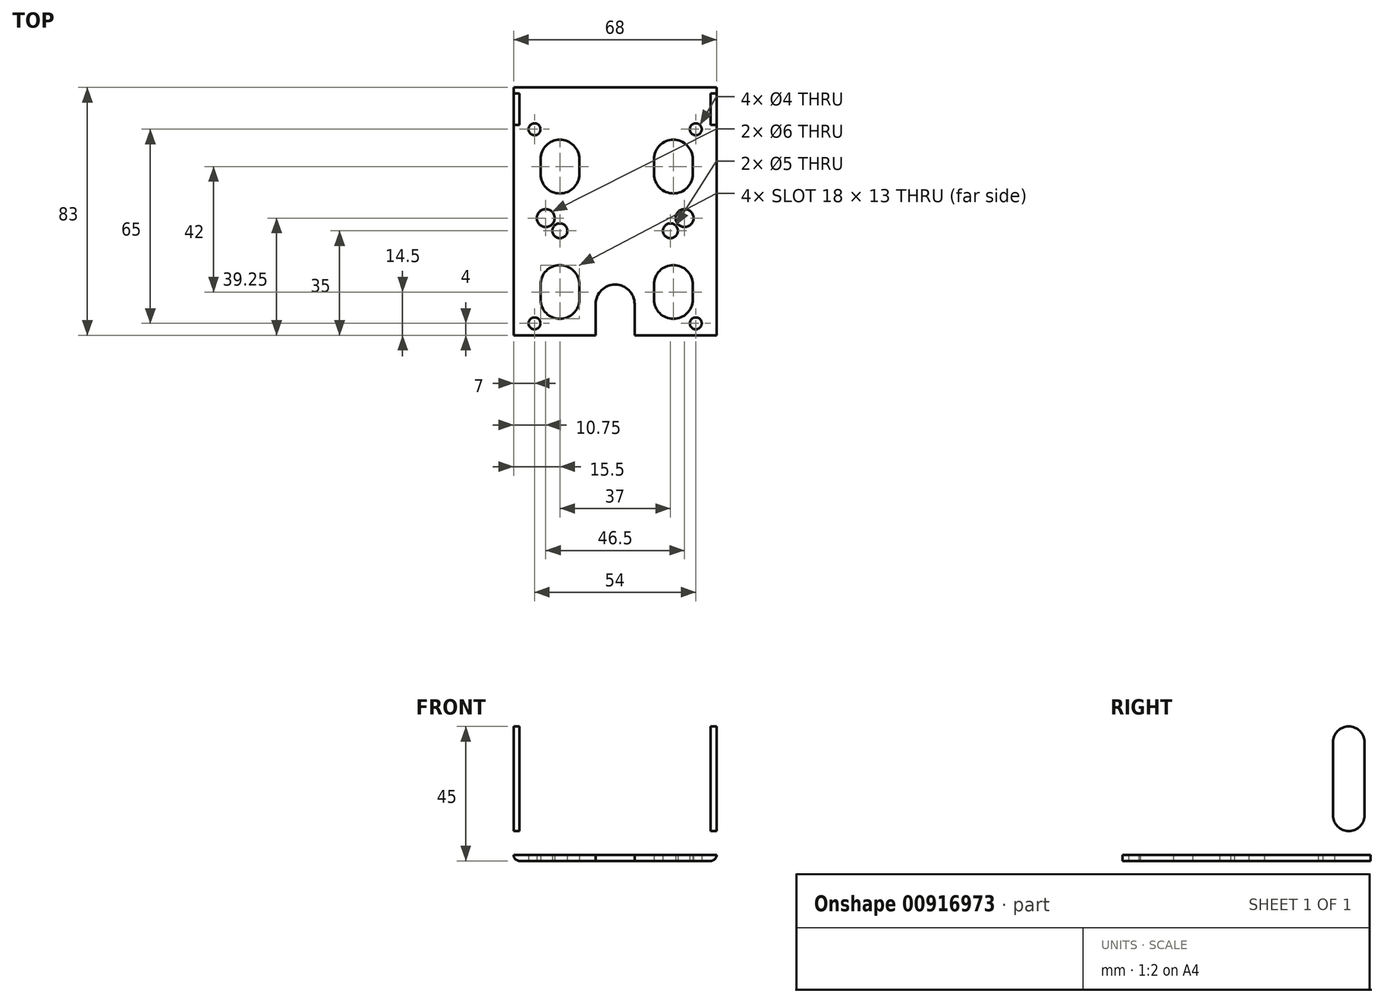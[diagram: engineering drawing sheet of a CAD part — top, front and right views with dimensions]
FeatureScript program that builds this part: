
annotation { "Feature Type Name" : "Feature", "Feature Type Description" : "" }
export const myFeature = defineFeature(function(context is Context, id is Id, definition is map)
    precondition{}
    {
        {
            var Q0;
            Q0=qCreatedBy(makeId("Front.planeOp"),FACE);
            var sketch = newSketch(context, id + "F0", { "sketchPlane" : qUnion([Q0])});
            skLineSegment(sketch, "E0.bottom", {"start": v(2, 0) * mm, "end": v(66, 0) * mm});
            skLineSegment(sketch, "E0.top", {"start": v(0, 60) * mm, "end": v(2, 60) * mm});
            skLineSegment(sketch, "E0.left", {"start": v(0, 2) * mm, "end": v(0, 60) * mm});
            skLineSegment(sketch, "E0.right", {"start": v(68, 2) * mm, "end": v(68, 60) * mm});
            skLineSegment(sketch, "E1.0", {"start": v(3, 2) * mm, "end": v(65, 2) * mm});
            skLineSegment(sketch, "E2.0", {"start": v(2, 3) * mm, "end": v(2, 60) * mm});
            skLineSegment(sketch, "E3.0", {"start": v(66, 3) * mm, "end": v(66, 60) * mm});
            skLineSegment(sketch, "E4.trimOffspring", {"start": v(66, 60) * mm, "end": v(68, 60) * mm});
            skPoint(sketch, "E5.visualSharp", {"position": v(0, 0) * mm});
            skArc(sketch, "E5.filletArc", {"start": v(0, 2) * mm, "mid": v(0.59, 0.59) * mm, "end": v(2, 0) * mm});
            skArc(sketch, "E6.filletArc", {"start": v(2, 3) * mm, "mid": v(2.3, 2.3) * mm, "end": v(3, 2) * mm});
            skPoint(sketch, "E7.visualSharp", {"position": v(66, 2) * mm});
            skArc(sketch, "E7.filletArc", {"start": v(65, 2) * mm, "mid": v(65.7, 2.3) * mm, "end": v(66, 3) * mm});
            skPoint(sketch, "E8.visualSharp", {"position": v(68, 0) * mm});
            skArc(sketch, "E8.filletArc", {"start": v(66, 0) * mm, "mid": v(67.41, 0.59) * mm, "end": v(68, 2) * mm});
            skSolve(sketch);
        }
        {
            var Q0;
            Q0=makeQuery(id+"F0.imprint","IMPRINT",FACE,{"disambiguationData":[TD([[makeQuery(id+"F0.imprint","IMPRINT",EDGE,{"derivedFrom":sQuery(id+"F0.wireOp",EDGE,"E0.bottom")}),1.0]])]});
            extrude(context, id + "F1", {"entities" : qUnion([Q0]), "depth" : 83 * mm, "offsetDistance" : 25 * mm});
        }
        {
            var Q0;
            Q0=makeQuery(id+"F1.opExtrude","SWEPT_FACE",FACE,{"disambiguationData":[OSD([sQuery(id+"F0.wireOp",EDGE,"E0.right")])]});
            var sketch = newSketch(context, id + "F2", { "sketchPlane" : qUnion([Q0])});
            skLineSegment(sketch, "E9.bottom", {"start": v(-75.75, 10) * mm, "end": v(-75.75, 10) * mm});
            skLineSegment(sketch, "E9.top", {"start": v(-75.75, 45) * mm, "end": v(-75.75, 45) * mm});
            skLineSegment(sketch, "E9.left", {"start": v(-81, 15.25) * mm, "end": v(-81, 39.75) * mm});
            skLineSegment(sketch, "E9.right", {"start": v(-70.5, 15.25) * mm, "end": v(-70.5, 39.75) * mm});
            skPoint(sketch, "E10.visualSharp", {"position": v(-81, 10) * mm});
            skArc(sketch, "E10.filletArc", {"start": v(-81, 15.25) * mm, "mid": v(-79.46, 11.54) * mm, "end": v(-75.75, 10) * mm});
            skPoint(sketch, "E11.visualSharp", {"position": v(-70.5, 10) * mm});
            skArc(sketch, "E11.filletArc", {"start": v(-75.75, 10) * mm, "mid": v(-72.04, 11.54) * mm, "end": v(-70.5, 15.25) * mm});
            skPoint(sketch, "E12.visualSharp", {"position": v(-81, 45) * mm});
            skArc(sketch, "E12.filletArc", {"start": v(-75.75, 45) * mm, "mid": v(-79.46, 43.46) * mm, "end": v(-81, 39.75) * mm});
            skPoint(sketch, "E13.visualSharp", {"position": v(-70.5, 45) * mm});
            skArc(sketch, "E13.filletArc", {"start": v(-70.5, 39.75) * mm, "mid": v(-72.04, 43.46) * mm, "end": v(-75.75, 45) * mm});
            skLineSegment(sketch, "E14", {"start": v(-41.5, 60) * mm, "end": v(-41.5, 21.27) * mm, "construction": true});
            skArc(sketch, "E15.MirrorCS", {"start": v(-12.5, 39.75) * mm, "mid": v(-10.96, 43.46) * mm, "end": v(-7.25, 45) * mm});
            skArc(sketch, "E16.MirrorCS", {"start": v(-7.25, 45) * mm, "mid": v(-3.54, 43.46) * mm, "end": v(-2, 39.75) * mm});
            skLineSegment(sketch, "E17.MirrorCS", {"start": v(-2, 15.25) * mm, "end": v(-2, 39.75) * mm});
            skLineSegment(sketch, "E18.MirrorCS", {"start": v(-12.5, 15.25) * mm, "end": v(-12.5, 39.75) * mm});
            skArc(sketch, "E19.MirrorCS", {"start": v(-7.25, 10) * mm, "mid": v(-10.96, 11.54) * mm, "end": v(-12.5, 15.25) * mm});
            skArc(sketch, "E20.MirrorCS", {"start": v(-2, 15.25) * mm, "mid": v(-3.54, 11.54) * mm, "end": v(-7.25, 10) * mm});
            skSolve(sketch);
        }
        {
            var Q0;
            Q0=makeQuery(id+"F2.imprint","IMPRINT",FACE,{"disambiguationData":[TD([[makeQuery(id+"F2.imprint","IMPRINT",EDGE,{"derivedFrom":sQuery(id+"F2.wireOp",EDGE,"E9.left")}),-1.0]])]});
            var Q1;
            Q1=makeQuery(id+"F2.imprint","IMPRINT",FACE,{"disambiguationData":[TD([[makeQuery(id+"F2.imprint","IMPRINT",EDGE,{"derivedFrom":sQuery(id+"F2.wireOp",EDGE,"E15.MirrorCS")}),-1.0]])]});
            extrude(context, id + "F3", {"entities" : qUnion([Q0, Q1]), "operationType" : NewBodyOperationType.REMOVE, "endBound" : BoundingType.THROUGH_ALL, "oppositeDirection" : true, "depth" : 25 * mm, "offsetDistance" : 25 * mm});
        }
        {
            var Q0;
            Q0=makeQuery(id+"F1.opExtrude","SWEPT_FACE",FACE,{"disambiguationData":[OSD([sQuery(id+"F0.wireOp",EDGE,"E0.bottom")])]});
            var sketch = newSketch(context, id + "F4", { "sketchPlane" : qUnion([Q0])});
            skLineSegment(sketch, "E21.bottom", {"start": v(15.5, 59.5) * mm, "end": v(15.5, 59.5) * mm});
            skLineSegment(sketch, "E21.top", {"start": v(15.5, 77.5) * mm, "end": v(15.5, 77.5) * mm});
            skLineSegment(sketch, "E21.left", {"start": v(9, 66) * mm, "end": v(9, 71) * mm});
            skLineSegment(sketch, "E21.right", {"start": v(22, 66) * mm, "end": v(22, 71) * mm});
            skPoint(sketch, "E22.visualSharp", {"position": v(9, 77.5) * mm});
            skArc(sketch, "E22.filletArc", {"start": v(15.5, 77.5) * mm, "mid": v(10.9, 75.6) * mm, "end": v(9, 71) * mm});
            skPoint(sketch, "E23.visualSharp", {"position": v(22, 77.5) * mm});
            skArc(sketch, "E23.filletArc", {"start": v(22, 71) * mm, "mid": v(20.1, 75.6) * mm, "end": v(15.5, 77.5) * mm});
            skPoint(sketch, "E24.visualSharp", {"position": v(22, 59.5) * mm});
            skArc(sketch, "E24.filletArc", {"start": v(15.5, 59.5) * mm, "mid": v(20.1, 61.4) * mm, "end": v(22, 66) * mm});
            skPoint(sketch, "E25.visualSharp", {"position": v(9, 59.5) * mm});
            skArc(sketch, "E25.filletArc", {"start": v(9, 66) * mm, "mid": v(10.9, 61.4) * mm, "end": v(15.5, 59.5) * mm});
            skArc(sketch, "E26.0.1.0", {"start": v(22, 29) * mm, "mid": v(20.1, 33.6) * mm, "end": v(15.5, 35.5) * mm});
            skArc(sketch, "E26.0.1.1", {"start": v(15.5, 35.5) * mm, "mid": v(10.9, 33.6) * mm, "end": v(9, 29) * mm});
            skLineSegment(sketch, "E26.0.1.2", {"start": v(9, 24) * mm, "end": v(9, 29) * mm});
            skLineSegment(sketch, "E26.0.1.3", {"start": v(22, 24) * mm, "end": v(22, 29) * mm});
            skArc(sketch, "E26.0.1.4", {"start": v(15.5, 17.5) * mm, "mid": v(20.1, 19.4) * mm, "end": v(22, 24) * mm});
            skArc(sketch, "E26.0.1.5", {"start": v(9, 24) * mm, "mid": v(10.9, 19.4) * mm, "end": v(15.5, 17.5) * mm});
            skArc(sketch, "E26.1.0.0", {"start": v(60, 71) * mm, "mid": v(58.1, 75.6) * mm, "end": v(53.5, 77.5) * mm});
            skArc(sketch, "E26.1.0.1", {"start": v(53.5, 77.5) * mm, "mid": v(48.9, 75.6) * mm, "end": v(47, 71) * mm});
            skLineSegment(sketch, "E26.1.0.2", {"start": v(47, 66) * mm, "end": v(47, 71) * mm});
            skLineSegment(sketch, "E26.1.0.3", {"start": v(60, 66) * mm, "end": v(60, 71) * mm});
            skArc(sketch, "E26.1.0.4", {"start": v(53.5, 59.5) * mm, "mid": v(58.1, 61.4) * mm, "end": v(60, 66) * mm});
            skArc(sketch, "E26.1.0.5", {"start": v(47, 66) * mm, "mid": v(48.9, 61.4) * mm, "end": v(53.5, 59.5) * mm});
            skArc(sketch, "E26.1.1.0", {"start": v(60, 29) * mm, "mid": v(58.1, 33.6) * mm, "end": v(53.5, 35.5) * mm});
            skArc(sketch, "E26.1.1.1", {"start": v(53.5, 35.5) * mm, "mid": v(48.9, 33.6) * mm, "end": v(47, 29) * mm});
            skLineSegment(sketch, "E26.1.1.2", {"start": v(47, 24) * mm, "end": v(47, 29) * mm});
            skLineSegment(sketch, "E26.1.1.3", {"start": v(60, 24) * mm, "end": v(60, 29) * mm});
            skArc(sketch, "E26.1.1.4", {"start": v(53.5, 17.5) * mm, "mid": v(58.1, 19.4) * mm, "end": v(60, 24) * mm});
            skArc(sketch, "E26.1.1.5", {"start": v(47, 24) * mm, "mid": v(48.9, 19.4) * mm, "end": v(53.5, 17.5) * mm});
            skLineSegment(sketch, "E26.direction1", {"start": v(15.5, 71) * mm, "end": v(53.5, 71) * mm, "construction": true});
            skLineSegment(sketch, "E26.direction2", {"start": v(15.5, 71) * mm, "end": v(15.5, 29) * mm, "construction": true});
            skSolve(sketch);
        }
        {
            var Q0;
            Q0=makeQuery(id+"F4.imprint","IMPRINT",FACE,{"disambiguationData":[TD([[makeQuery(id+"F4.imprint","IMPRINT",EDGE,{"derivedFrom":sQuery(id+"F4.wireOp",EDGE,"E21.left")}),-1.0]])]});
            var Q1;
            Q1=makeQuery(id+"F4.imprint","IMPRINT",FACE,{"disambiguationData":[TD([[makeQuery(id+"F4.imprint","IMPRINT",EDGE,{"derivedFrom":sQuery(id+"F4.wireOp",EDGE,"E26.1.0.0")}),1.0]])]});
            var Q2;
            Q2=makeQuery(id+"F4.imprint","IMPRINT",FACE,{"disambiguationData":[TD([[makeQuery(id+"F4.imprint","IMPRINT",EDGE,{"derivedFrom":sQuery(id+"F4.wireOp",EDGE,"E26.1.1.0")}),1.0]])]});
            var Q3;
            Q3=makeQuery(id+"F4.imprint","IMPRINT",FACE,{"disambiguationData":[TD([[makeQuery(id+"F4.imprint","IMPRINT",EDGE,{"derivedFrom":sQuery(id+"F4.wireOp",EDGE,"E26.0.1.0")}),1.0]])]});
            extrude(context, id + "F5", {"entities" : qUnion([Q0, Q1, Q2, Q3]), "operationType" : NewBodyOperationType.REMOVE, "endBound" : BoundingType.THROUGH_ALL, "oppositeDirection" : true, "depth" : 25 * mm, "offsetDistance" : 25 * mm});
        }
        {
            var Q0;
            Q0=makeQuery(id+"F1.opExtrude","SWEPT_FACE",FACE,{"disambiguationData":[OSD([sQuery(id+"F0.wireOp",EDGE,"E0.bottom")])]});
            var sketch = newSketch(context, id + "F6", { "sketchPlane" : qUnion([Q0])});
            skCircle(sketch, "E27", {"center": v(10.75, 43.75) * mm, "radius": 3 * mm});
            skCircle(sketch, "E28", {"center": v(57.25, 43.75) * mm, "radius": 3 * mm});
            skSolve(sketch);
        }
        {
            var Q0;
            Q0=makeQuery(id+"F6.imprint","IMPRINT",FACE,{"disambiguationData":[TD([[makeQuery(id+"F6.imprint","IMPRINT",EDGE,{"derivedFrom":sQuery(id+"F6.wireOp",EDGE,"E28")}),1.0]])]});
            var Q1;
            Q1=makeQuery(id+"F6.imprint","IMPRINT",FACE,{"disambiguationData":[TD([[makeQuery(id+"F6.imprint","IMPRINT",EDGE,{"derivedFrom":sQuery(id+"F6.wireOp",EDGE,"E27")}),1.0]])]});
            extrude(context, id + "F7", {"entities" : qUnion([Q0, Q1]), "operationType" : NewBodyOperationType.REMOVE, "endBound" : BoundingType.THROUGH_ALL, "oppositeDirection" : true, "depth" : 25 * mm, "offsetDistance" : 25 * mm});
        }
        {
            var Q0;
            Q0=makeQuery(id+"F1.opExtrude","SWEPT_FACE",FACE,{"disambiguationData":[OSD([sQuery(id+"F0.wireOp",EDGE,"E0.bottom")])]});
            var sketch = newSketch(context, id + "F8", { "sketchPlane" : qUnion([Q0])});
            skCircle(sketch, "E29", {"center": v(15.5, 48) * mm, "radius": 2.5 * mm});
            skCircle(sketch, "E30", {"center": v(52.5, 48) * mm, "radius": 2.5 * mm});
            skSolve(sketch);
        }
        {
            var Q0;
            Q0=makeQuery(id+"F8.imprint","IMPRINT",FACE,{"disambiguationData":[TD([[makeQuery(id+"F8.imprint","IMPRINT",EDGE,{"derivedFrom":sQuery(id+"F8.wireOp",EDGE,"E29")}),1.0]])]});
            var Q1;
            Q1=makeQuery(id+"F8.imprint","IMPRINT",FACE,{"disambiguationData":[TD([[makeQuery(id+"F8.imprint","IMPRINT",EDGE,{"derivedFrom":sQuery(id+"F8.wireOp",EDGE,"E30")}),1.0]])]});
            extrude(context, id + "F9", {"entities" : qUnion([Q0, Q1]), "operationType" : NewBodyOperationType.REMOVE, "endBound" : BoundingType.THROUGH_ALL, "oppositeDirection" : true, "depth" : 25 * mm, "offsetDistance" : 25 * mm});
        }
        {
            var Q0;
            Q0=makeQuery(id+"F1.opExtrude","SWEPT_FACE",FACE,{"disambiguationData":[OSD([sQuery(id+"F0.wireOp",EDGE,"E0.bottom")])]});
            var sketch = newSketch(context, id + "F10", { "sketchPlane" : qUnion([Q0])});
            skCircle(sketch, "E31", {"center": v(7, 79) * mm, "radius": 2 * mm});
            skCircle(sketch, "E32", {"center": v(61, 79) * mm, "radius": 2 * mm});
            skCircle(sketch, "E33", {"center": v(7, 14) * mm, "radius": 2 * mm});
            skCircle(sketch, "E34", {"center": v(61, 14) * mm, "radius": 2 * mm});
            skSolve(sketch);
        }
        {
            var Q0;
            Q0 = qSketchRegion(id + "F10", true);
            extrude(context, id + "F11", {"entities" : qUnion([Q0]), "operationType" : NewBodyOperationType.REMOVE, "endBound" : BoundingType.THROUGH_ALL, "oppositeDirection" : true, "depth" : 25 * mm, "offsetDistance" : 25 * mm});
        }
        {
            var Q0;
            Q0=makeQuery(id+"F1.opExtrude","SWEPT_FACE",FACE,{"disambiguationData":[OSD([sQuery(id+"F0.wireOp",EDGE,"E0.bottom")])]});
            var sketch = newSketch(context, id + "F12", { "sketchPlane" : qUnion([Q0])});
            skLineSegment(sketch, "E35", {"start": v(34, 83) * mm, "end": v(34, 73.09) * mm, "construction": true});
            skLineSegment(sketch, "E36.0", {"start": v(27.5, 83) * mm, "end": v(27.5, 72.5) * mm});
            skLineSegment(sketch, "E37.0", {"start": v(40.5, 83) * mm, "end": v(40.5, 72.5) * mm});
            skLineSegment(sketch, "E38", {"start": v(34, 66) * mm, "end": v(34, 66) * mm});
            skPoint(sketch, "E39.visualSharp", {"position": v(27.5, 66) * mm});
            skArc(sketch, "E39.filletArc", {"start": v(27.5, 72.5) * mm, "mid": v(29.4, 67.9) * mm, "end": v(34, 66) * mm});
            skPoint(sketch, "E40.visualSharp", {"position": v(40.5, 66) * mm});
            skArc(sketch, "E40.filletArc", {"start": v(34, 66) * mm, "mid": v(38.6, 67.9) * mm, "end": v(40.5, 72.5) * mm});
            skSolve(sketch);
        }
        {
            var Q0;
            {var subQ1=sQuery(id+"F12.wireOp",EDGE,"E36.0");Q0=makeQuery(id+"F12.imprint","IMPRINT",FACE,{"disambiguationData":[TD([[makeQuery(id+"F12.imprint","IMPRINT",EDGE,{"derivedFrom":subQ1}),1.0]])]});}
            extrude(context, id + "F13", {"entities" : qUnion([Q0]), "operationType" : NewBodyOperationType.REMOVE, "endBound" : BoundingType.THROUGH_ALL, "oppositeDirection" : true, "depth" : 25 * mm, "offsetDistance" : 25 * mm});
        }
        {
            var Q0;
            Q0=makeQuery(id+"F1.opExtrude","SWEPT_FACE",FACE,{"disambiguationData":[OSD([sQuery(id+"F0.wireOp",EDGE,"E0.left")])]});
            var sketch = newSketch(context, id + "F14", { "sketchPlane" : qUnion([Q0])});
            skCircle(sketch, "E41", {"center": v(76, 54) * mm, "radius": 3 * mm});
            skCircle(sketch, "E42", {"center": v(7, 54) * mm, "radius": 3 * mm});
            skSolve(sketch);
        }
        {
            var Q0;
            Q0=makeQuery(id+"F14.imprint","IMPRINT",FACE,{"disambiguationData":[TD([[makeQuery(id+"F14.imprint","IMPRINT",EDGE,{"derivedFrom":sQuery(id+"F14.wireOp",EDGE,"E42")}),1.0]])]});
            var Q1;
            Q1=makeQuery(id+"F14.imprint","IMPRINT",FACE,{"disambiguationData":[TD([[makeQuery(id+"F14.imprint","IMPRINT",EDGE,{"derivedFrom":sQuery(id+"F14.wireOp",EDGE,"E41")}),1.0]])]});
            extrude(context, id + "F15", {"entities" : qUnion([Q0, Q1]), "operationType" : NewBodyOperationType.REMOVE, "endBound" : BoundingType.THROUGH_ALL, "oppositeDirection" : true, "depth" : 25 * mm, "offsetDistance" : 25 * mm});
        }
    });
